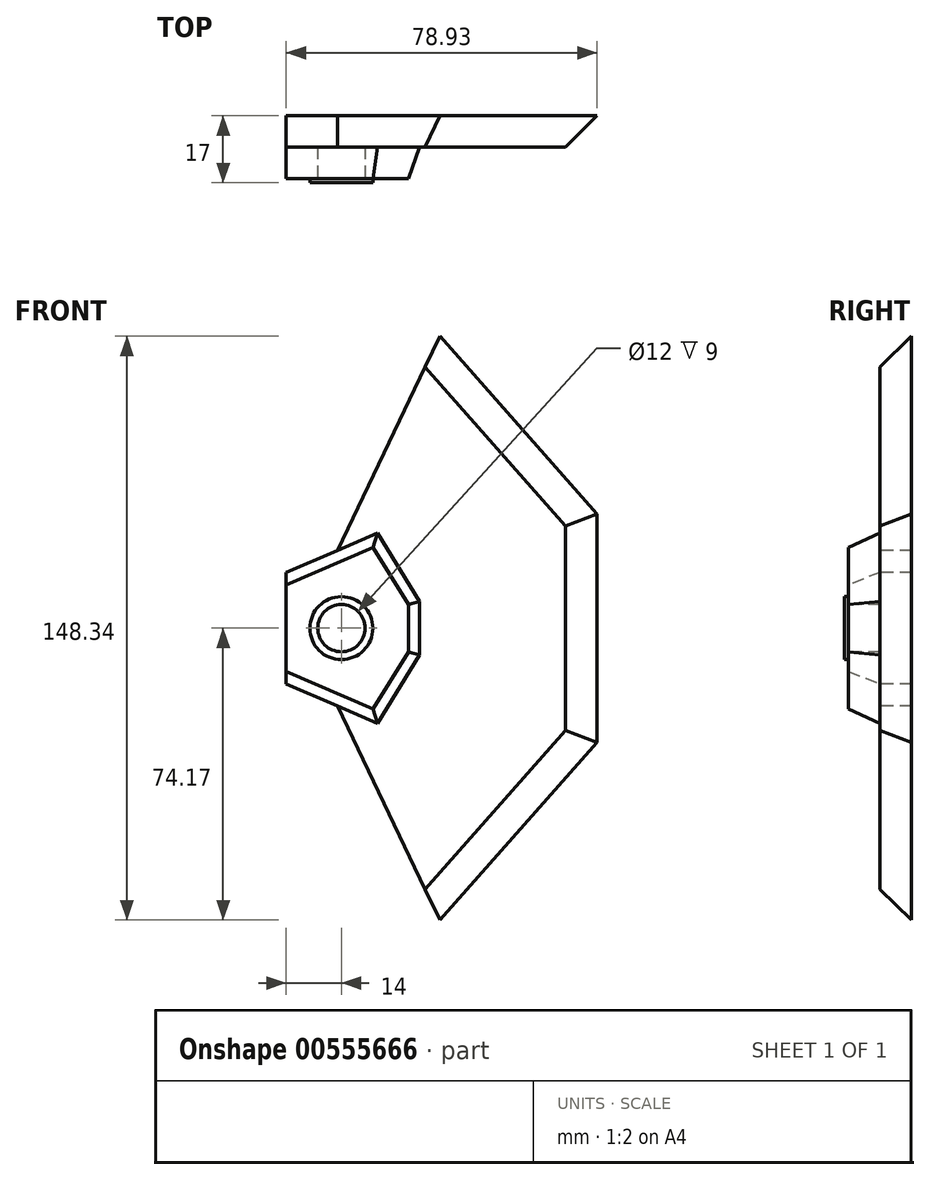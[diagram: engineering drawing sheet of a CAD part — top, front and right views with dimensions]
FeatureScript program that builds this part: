
annotation { "Feature Type Name" : "Feature", "Feature Type Description" : "" }
export const myFeature = defineFeature(function(context is Context, id is Id, definition is map)
    precondition{}
    {
        {
            var Q0;
            Q0=qCreatedBy(makeId("Front.planeOp"),FACE);
            var sketch = newSketch(context, id + "F0", { "sketchPlane" : qUnion([Q0])});
            skLineSegment(sketch, "E0", {"start": v(0, 0) * mm, "end": v(0, 11) * mm});
            skLineSegment(sketch, "E1", {"start": v(0, 11) * mm, "end": v(22.04, 20.5) * mm});
            skLineSegment(sketch, "E2", {"start": v(22.04, 20.5) * mm, "end": v(31, 6) * mm});
            skLineSegment(sketch, "E3", {"start": v(31, 6) * mm, "end": v(31, 0) * mm});
            skLineSegment(sketch, "E4.MirrorCS", {"start": v(0, 0) * mm, "end": v(0, -11) * mm});
            skLineSegment(sketch, "E5.MirrorCS", {"start": v(0, -11) * mm, "end": v(22.04, -20.5) * mm});
            skLineSegment(sketch, "E6.MirrorCS", {"start": v(22.04, -20.5) * mm, "end": v(31, -6) * mm});
            skLineSegment(sketch, "E7.MirrorCS", {"start": v(31, -6) * mm, "end": v(31, 0) * mm});
            skSolve(sketch);
        }
        {
            var Q0;
            Q0 = qSketchRegion(id + "F0", true);
            extrude(context, id + "F1", {"entities" : qUnion([Q0]), "oppositeDirection" : true, "depth" : 8 * mm, "offsetDistance" : 25 * mm, "hasDraft" : true, "draftAngle" : 20 * degree});
        }
        {
            var Q0;
            Q0=qCreatedBy(makeId("Front.planeOp"),FACE);
            var sketch = newSketch(context, id + "F2", { "sketchPlane" : qUnion([Q0])});
            skLineSegment(sketch, "E8.bottom", {"start": v(0, 25.58) * mm, "end": v(-14.83, 25.58) * mm});
            skLineSegment(sketch, "E8.top", {"start": v(0, -28.58) * mm, "end": v(-14.83, -28.58) * mm});
            skLineSegment(sketch, "E8.left", {"start": v(0, 25.58) * mm, "end": v(0, -28.58) * mm});
            skLineSegment(sketch, "E8.right", {"start": v(-14.83, 25.58) * mm, "end": v(-14.83, -28.58) * mm});
            skSolve(sketch);
        }
        {
            var Q0;
            Q0=makeQuery(id+"F2.imprint","IMPRINT",FACE,{"disambiguationData":[TD([[makeQuery(id+"F2.imprint","IMPRINT",EDGE,{"derivedFrom":sQuery(id+"F2.wireOp",EDGE,"E8.bottom")}),1.0]])]});
            extrude(context, id + "F3", {"entities" : qUnion([Q0]), "operationType" : NewBodyOperationType.REMOVE, "endBound" : BoundingType.THROUGH_ALL, "oppositeDirection" : true, "depth" : 25 * mm, "offsetDistance" : 25 * mm});
        }
        {
            var Q0;
            Q0=qCreatedBy(makeId("Front.planeOp"),FACE);
            var sketch = newSketch(context, id + "F4", { "sketchPlane" : qUnion([Q0])});
            skCircle(sketch, "E9", {"center": v(14, 0) * mm, "radius": 6 * mm});
            skCircle(sketch, "E10", {"center": v(14, 0) * mm, "radius": 8 * mm});
            skSolve(sketch);
        }
        {
            var Q0;
            Q0=makeQuery(id+"F4.imprint","IMPRINT",FACE,{"disambiguationData":[TD([[makeQuery(id+"F4.imprint","IMPRINT",EDGE,{"derivedFrom":sQuery(id+"F4.wireOp",EDGE,"E9")}),1.0]])]});
            extrude(context, id + "F5", {"entities" : qUnion([Q0]), "operationType" : NewBodyOperationType.REMOVE, "endBound" : BoundingType.THROUGH_ALL, "oppositeDirection" : true, "depth" : 25 * mm, "offsetDistance" : 25 * mm, "hasSecondDirection" : true, "secondDirectionBound" : BoundingType.THROUGH_ALL, "secondDirectionOppositeDirection" : false, "secondDirectionDepth" : 25 * mm});
        }
        {
            var Q0;
            Q0 = qSketchRegion(id + "F4", true);
            extrude(context, id + "F6", {"entities" : qUnion([Q0]), "operationType" : NewBodyOperationType.ADD, "depth" : 1 * mm, "offsetDistance" : 25 * mm});
        }
        {
            var Q0;
            Q0=qCreatedBy(makeId("Front.planeOp"),FACE);
            var sketch = newSketch(context, id + "F7", { "sketchPlane" : qUnion([Q0])});
            skLineSegment(sketch, "E11", {"start": v(0, 14.17) * mm, "end": v(13, 19.77) * mm});
            skLineSegment(sketch, "E12", {"start": v(13, 19.77) * mm, "end": v(39, 74.17) * mm});
            skLineSegment(sketch, "E13", {"start": v(39, 74.17) * mm, "end": v(78.93, 29) * mm});
            skLineSegment(sketch, "E14.MirrorCS", {"start": v(0, -14.17) * mm, "end": v(13, -19.77) * mm});
            skLineSegment(sketch, "E15.MirrorCS", {"start": v(13, -19.77) * mm, "end": v(39, -74.17) * mm});
            skLineSegment(sketch, "E16.MirrorCS", {"start": v(39, -74.17) * mm, "end": v(78.93, -29) * mm});
            skLineSegment(sketch, "E17", {"start": v(78.93, 29) * mm, "end": v(78.93, -29) * mm});
            skLineSegment(sketch, "E18", {"start": v(0, 14.17) * mm, "end": v(0, -14.17) * mm});
            skSolve(sketch);
        }
        {
            var Q0;
            Q0=makeQuery(id+"F1.opExtrude","CAP_FACE",FACE,{"disambiguationData":[OSD([sQuery(id+"F0.wireOp",EDGE,"E0"),sQuery(id+"F0.wireOp",EDGE,"E1"),sQuery(id+"F0.wireOp",EDGE,"E2"),sQuery(id+"F0.wireOp",EDGE,"E3"),sQuery(id+"F0.wireOp",EDGE,"E4.MirrorCS"),sQuery(id+"F0.wireOp",EDGE,"E5.MirrorCS"),sQuery(id+"F0.wireOp",EDGE,"E6.MirrorCS"),sQuery(id+"F0.wireOp",EDGE,"E7.MirrorCS")])],"isStart":false});
            var sketch = newSketch(context, id + "F8", { "sketchPlane" : qUnion([Q0])});
            skLineSegment(sketch, "E19.0.0", {"start": v(-13, -19.77) * mm, "end": v(-39, -74.17) * mm});
            skLineSegment(sketch, "E19.0.1", {"start": v(-39, -74.17) * mm, "end": v(-78.93, -29) * mm});
            skLineSegment(sketch, "E19.0.2", {"start": v(-78.93, -29) * mm, "end": v(-78.93, 29) * mm});
            skLineSegment(sketch, "E19.0.3", {"start": v(-78.93, 29) * mm, "end": v(-39, 74.17) * mm});
            skLineSegment(sketch, "E19.0.4", {"start": v(-39, 74.17) * mm, "end": v(-13, 19.77) * mm});
            skLineSegment(sketch, "E19.0.5", {"start": v(-13, 19.77) * mm, "end": v(0, 14.17) * mm});
            skLineSegment(sketch, "E19.0.6", {"start": v(0, 14.17) * mm, "end": v(0, -14.17) * mm});
            skLineSegment(sketch, "E19.0.7", {"start": v(0, -14.17) * mm, "end": v(-13, -19.77) * mm});
            skSolve(sketch);
        }
        {
            var Q0;
            Q0 = qSketchRegion(id + "F8", true);
            extrude(context, id + "F9", {"entities" : qUnion([Q0]), "operationType" : NewBodyOperationType.ADD, "depth" : 8 * mm, "offsetDistance" : 25 * mm});
        }
        {
            var Q0;
            Q0=makeQuery(id+"F9.opExtrude","CAP_EDGE",EDGE,{"disambiguationData":[OSD([sQuery(id+"F8.wireOp",EDGE,"E19.0.3")])],"isStart":true});
            var Q1;
            Q1=makeQuery(id+"F9.opExtrude","CAP_EDGE",EDGE,{"disambiguationData":[OSD([sQuery(id+"F8.wireOp",EDGE,"E19.0.2")])],"isStart":true});
            var Q2;
            Q2=makeQuery(id+"F9.opExtrude","CAP_EDGE",EDGE,{"disambiguationData":[OSD([sQuery(id+"F8.wireOp",EDGE,"E19.0.1")])],"isStart":true});
            chamfer(context, id + "F10", {"entities" : qUnion([Q0, Q1, Q2]), "width" : 8 * mm, "tangentPropagation" : true});
        }
    });
